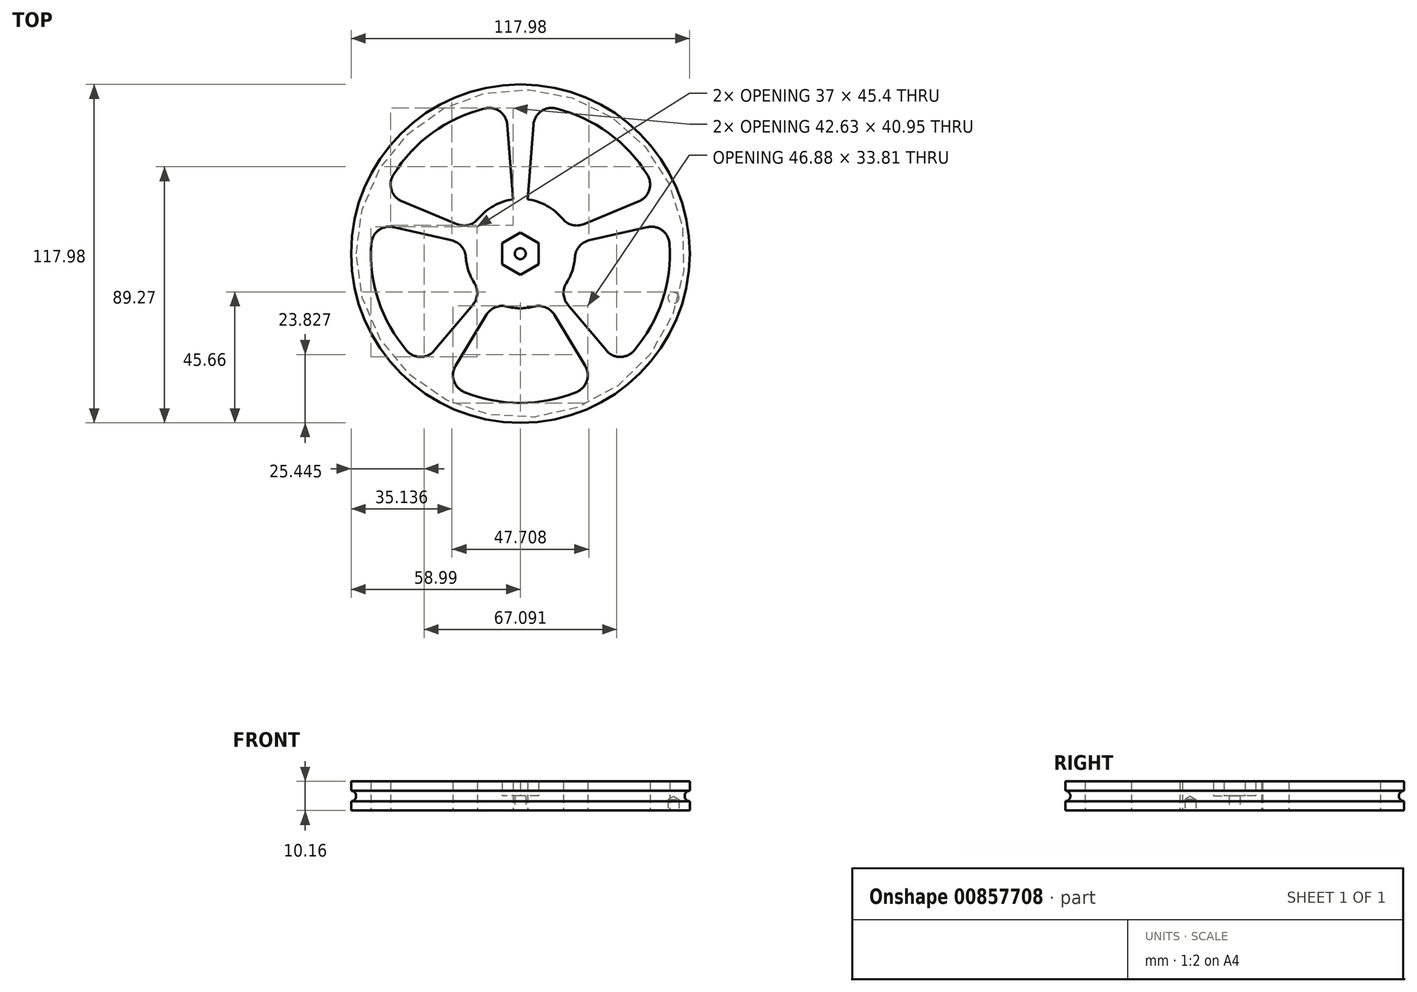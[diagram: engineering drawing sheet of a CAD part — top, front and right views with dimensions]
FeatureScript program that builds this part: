
annotation { "Feature Type Name" : "Feature", "Feature Type Description" : "" }
export const myFeature = defineFeature(function(context is Context, id is Id, definition is map)
    precondition{}
    {
        {
            var Q0;
            Q0=qCreatedBy(makeId("Top.planeOp"),FACE);
            var sketch = newSketch(context, id + "F0", { "sketchPlane" : qUnion([Q0])});
            skLineSegment(sketch, "E0.0", {"start": v(-0.03, -7.4) * mm, "end": v(-6.4, -3.71) * mm});
            skLineSegment(sketch, "E0.1", {"start": v(-6.4, -3.71) * mm, "end": v(-6.4, 3.65) * mm});
            skLineSegment(sketch, "E0.2", {"start": v(-6.4, 3.65) * mm, "end": v(-0.03, 7.34) * mm});
            skLineSegment(sketch, "E0.3", {"start": v(-0.03, 7.34) * mm, "end": v(6.35, 3.65) * mm});
            skLineSegment(sketch, "E0.4", {"start": v(6.35, 3.65) * mm, "end": v(6.35, -3.71) * mm});
            skLineSegment(sketch, "E0.5", {"start": v(6.35, -3.71) * mm, "end": v(-0.03, -7.4) * mm});
            skCircle(sketch, "E1", {"center": v(-0.03, -0.03) * mm, "radius": 1.9 * mm});
            skCircle(sketch, "E2", {"center": v(0, 0) * mm, "radius": 59 * mm});
            skArc(sketch, "E3", {"start": v(44.24, 27.46) * mm, "mid": v(30.58, 42.14) * mm, "end": v(12.39, 50.57) * mm});
            skArc(sketch, "E4", {"start": v(-4.77, -18.44) * mm, "mid": v(0, -19.05) * mm, "end": v(4.77, -18.44) * mm});
            skLineSegment(sketch, "E5", {"start": v(0, 0) * mm, "end": v(0, 52.07) * mm, "construction": true});
            skLineSegment(sketch, "E6", {"start": v(16.52, -17.8) * mm, "end": v(29.91, -33.76) * mm});
            skLineSegment(sketch, "E7", {"start": v(22.05, 10.27) * mm, "end": v(41.28, 18.24) * mm});
            skLineSegment(sketch, "E8.MirrorCS", {"start": v(11.79, -21.3) * mm, "end": v(22.56, -39.1) * mm});
            skLineSegment(sketch, "E9.MirrorCS", {"start": v(23.94, 4.6) * mm, "end": v(44.21, 9.2) * mm});
            skLineSegment(sketch, "E10", {"start": v(4.55, 44.9) * mm, "end": v(2.54, 18.88) * mm});
            skLineSegment(sketch, "E11.MirrorCS", {"start": v(-4.55, 44.9) * mm, "end": v(-2.54, 18.88) * mm});
            skLineSegment(sketch, "E12.MirrorCS", {"start": v(-22.05, 10.27) * mm, "end": v(-41.28, 18.24) * mm});
            skLineSegment(sketch, "E13.MirrorCS", {"start": v(-23.94, 4.6) * mm, "end": v(-44.21, 9.2) * mm});
            skLineSegment(sketch, "E14.MirrorCS", {"start": v(-16.52, -17.8) * mm, "end": v(-29.91, -33.76) * mm});
            skLineSegment(sketch, "E15.MirrorCS", {"start": v(-11.79, -21.3) * mm, "end": v(-22.56, -39.1) * mm});
            skArc(sketch, "E16.trimOffspring", {"start": v(39.6, -33.8) * mm, "mid": v(49.42, -16.39) * mm, "end": v(51.96, 3.44) * mm});
            skArc(sketch, "E17.trimOffspring", {"start": v(-19.5, -48.28) * mm, "mid": v(0, -52.07) * mm, "end": v(19.5, -48.28) * mm});
            skArc(sketch, "E18.trimOffspring", {"start": v(-51.96, 3.44) * mm, "mid": v(-49.42, -16.39) * mm, "end": v(-39.6, -33.8) * mm});
            skArc(sketch, "E19.trimOffspring", {"start": v(-12.39, 50.57) * mm, "mid": v(-30.58, 42.14) * mm, "end": v(-44.24, 27.46) * mm});
            skArc(sketch, "E20.trimOffspring", {"start": v(-19.01, -1.2) * mm, "mid": v(-18.1, -5.93) * mm, "end": v(-16.04, -10.28) * mm});
            skArc(sketch, "E21.trimOffspring", {"start": v(-2.54, 18.88) * mm, "mid": v(-9.27, 16.64) * mm, "end": v(-14.71, 12.1) * mm});
            skArc(sketch, "E22.trimOffspring", {"start": v(14.71, 12.1) * mm, "mid": v(9.27, 16.64) * mm, "end": v(2.54, 18.88) * mm});
            skPoint(sketch, "E23.visualSharp", {"position": v(-47.7, 20.9) * mm});
            skArc(sketch, "E23.filletArc", {"start": v(-44.24, 27.46) * mm, "mid": v(-44.9, 22.17) * mm, "end": v(-41.28, 18.24) * mm});
            skPoint(sketch, "E24.visualSharp", {"position": v(-50.95, 10.74) * mm});
            skArc(sketch, "E24.filletArc", {"start": v(-44.21, 9.2) * mm, "mid": v(-49.42, 8.1) * mm, "end": v(-51.96, 3.44) * mm});
            skPoint(sketch, "E25.visualSharp", {"position": v(-34.4, -39.1) * mm});
            skArc(sketch, "E25.filletArc", {"start": v(-39.6, -33.8) * mm, "mid": v(-34.75, -36.03) * mm, "end": v(-29.91, -33.76) * mm});
            skPoint(sketch, "E26.visualSharp", {"position": v(-26.15, -45.03) * mm});
            skArc(sketch, "E26.filletArc", {"start": v(-22.56, -39.1) * mm, "mid": v(-23.15, -44.4) * mm, "end": v(-19.5, -48.28) * mm});
            skPoint(sketch, "E27.visualSharp", {"position": v(26.15, -45.03) * mm});
            skArc(sketch, "E27.filletArc", {"start": v(19.5, -48.28) * mm, "mid": v(23.15, -44.4) * mm, "end": v(22.56, -39.1) * mm});
            skPoint(sketch, "E28.visualSharp", {"position": v(34.4, -39.1) * mm});
            skArc(sketch, "E28.filletArc", {"start": v(29.91, -33.76) * mm, "mid": v(34.75, -36.03) * mm, "end": v(39.6, -33.8) * mm});
            skPoint(sketch, "E29.visualSharp", {"position": v(50.95, 10.74) * mm});
            skArc(sketch, "E29.filletArc", {"start": v(51.96, 3.44) * mm, "mid": v(49.42, 8.1) * mm, "end": v(44.21, 9.2) * mm});
            skPoint(sketch, "E30.visualSharp", {"position": v(47.7, 20.9) * mm});
            skArc(sketch, "E30.filletArc", {"start": v(41.28, 18.24) * mm, "mid": v(44.9, 22.17) * mm, "end": v(44.24, 27.46) * mm});
            skPoint(sketch, "E31.visualSharp", {"position": v(5.08, 51.82) * mm});
            skArc(sketch, "E31.filletArc", {"start": v(12.39, 50.57) * mm, "mid": v(7.15, 49.55) * mm, "end": v(4.55, 44.9) * mm});
            skPoint(sketch, "E32.visualSharp", {"position": v(-5.08, 51.82) * mm});
            skArc(sketch, "E32.filletArc", {"start": v(-4.55, 44.9) * mm, "mid": v(-7.15, 49.55) * mm, "end": v(-12.39, 50.57) * mm});
            skPoint(sketch, "E33.visualSharp", {"position": v(-17.17, 8.25) * mm});
            skArc(sketch, "E33.filletArc", {"start": v(-22.05, 10.27) * mm, "mid": v(-18.08, 9.98) * mm, "end": v(-14.71, 12.1) * mm});
            skPoint(sketch, "E34.visualSharp", {"position": v(-18.74, 3.42) * mm});
            skArc(sketch, "E34.filletArc", {"start": v(-19.01, -1.2) * mm, "mid": v(-20.51, 2.52) * mm, "end": v(-23.94, 4.6) * mm});
            skPoint(sketch, "E35.visualSharp", {"position": v(-13.15, -13.78) * mm});
            skArc(sketch, "E35.filletArc", {"start": v(-16.52, -17.8) * mm, "mid": v(-15.04, -14.12) * mm, "end": v(-16.04, -10.28) * mm});
            skPoint(sketch, "E36.visualSharp", {"position": v(-9.04, -16.77) * mm});
            skArc(sketch, "E36.filletArc", {"start": v(-4.77, -18.44) * mm, "mid": v(-8.75, -18.71) * mm, "end": v(-11.79, -21.3) * mm});
            skPoint(sketch, "E37.visualSharp", {"position": v(18.74, 3.42) * mm});
            skArc(sketch, "E37.filletArc", {"start": v(23.94, 4.6) * mm, "mid": v(20.51, 2.52) * mm, "end": v(19.01, -1.2) * mm});
            skPoint(sketch, "E38.visualSharp", {"position": v(17.17, 8.25) * mm});
            skArc(sketch, "E38.filletArc", {"start": v(14.71, 12.1) * mm, "mid": v(18.08, 9.98) * mm, "end": v(22.05, 10.27) * mm});
            skArc(sketch, "E39.trimOffspring", {"start": v(16.04, -10.28) * mm, "mid": v(18.1, -5.93) * mm, "end": v(19.01, -1.2) * mm});
            skPoint(sketch, "E40.visualSharp", {"position": v(9.04, -16.77) * mm});
            skArc(sketch, "E40.filletArc", {"start": v(11.79, -21.3) * mm, "mid": v(8.75, -18.71) * mm, "end": v(4.77, -18.44) * mm});
            skPoint(sketch, "E41.visualSharp", {"position": v(13.15, -13.78) * mm});
            skArc(sketch, "E41.filletArc", {"start": v(16.04, -10.28) * mm, "mid": v(15.04, -14.12) * mm, "end": v(16.52, -17.8) * mm});
            skPoint(sketch, "E42.endSnap0", {"position": v(49.42, -16.39) * mm});
            skPoint(sketch, "E43", {"position": v(53.34, -15.43) * mm});
            skCircle(sketch, "E44", {"center": v(53.34, -15.43) * mm, "radius": 1.9 * mm});
            skSolve(sketch);
        }
        {
            var Q0;
            Q0=makeQuery(id+"F0.imprint","IMPRINT",FACE,{"disambiguationData":[TD([[makeQuery(id+"F0.imprint","IMPRINT",EDGE,{"derivedFrom":sQuery(id+"F0.wireOp",EDGE,"E0.0")}),-1.0]])]});
            extrude(context, id + "F1", {"entities" : qUnion([Q0]), "depth" : 5.08 * mm, "offsetDistance" : 25.4 * mm});
        }
        {
            var Q0;
            Q0=makeQuery(id+"F0.imprint","IMPRINT",FACE,{"disambiguationData":[TD([[makeQuery(id+"F0.imprint","IMPRINT",EDGE,{"derivedFrom":sQuery(id+"F0.wireOp",EDGE,"E0.0")}),1.0]])]});
            var Q1;
            Q1=makeQuery(id+"F0.imprint","IMPRINT",FACE,{"disambiguationData":[TD([[makeQuery(id+"F0.imprint","IMPRINT",EDGE,{"derivedFrom":sQuery(id+"F0.wireOp",EDGE,"E44")}),1.0]])]});
            extrude(context, id + "F2", {"entities" : qUnion([Q0, Q1]), "operationType" : NewBodyOperationType.ADD, "depth" : 10.16 * mm, "offsetDistance" : 25.4 * mm});
        }
        {
            var Q0;
            Q0=qCreatedBy(makeId("Front.planeOp"),FACE);
            var sketch = newSketch(context, id + "F3", { "sketchPlane" : qUnion([Q0])});
            skCircle(sketch, "E45", {"center": v(59.06, 5.08) * mm, "radius": 1.84 * mm});
            skSolve(sketch);
        }
        {
            var Q0;
            Q0=qCreatedBy(makeId("Front.planeOp"),FACE);
            var sketch = newSketch(context, id + "F4", { "sketchPlane" : qUnion([Q0])});
            skLineSegment(sketch, "E46", {"start": v(0, -19.08) * mm, "end": v(0, 27.89) * mm});
            skSolve(sketch);
        }
        {
            var Q0;
            Q0 = qSketchRegion(id + "F3", true);
            var Q1;
            Q1=sQuery(id+"F4.wireOp",EDGE,"E46");
            revolve(context, id + "F5", {"surfaceOperationType" : NewSurfaceOperationType.NEW, "entities" : qUnion([Q0]), "axis" : qUnion([Q1]), "revolveType" : RevolveType.FULL});
        }
        {
            var Q0;
            Q0=makeQuery(id+"F5.opRevolve","SWEPT_BODY",BODY,{"disambiguationData":[OSD([sQuery(id+"F3.wireOp",EDGE,"E45")])]});
            var Q1;
            Q1=makeQuery(id+"F1.opExtrude","SWEPT_BODY",BODY,{"disambiguationData":[OSD([sQuery(id+"F0.wireOp",EDGE,"E0.0"),sQuery(id+"F0.wireOp",EDGE,"E0.1"),sQuery(id+"F0.wireOp",EDGE,"E0.2"),sQuery(id+"F0.wireOp",EDGE,"E0.3"),sQuery(id+"F0.wireOp",EDGE,"E0.4"),sQuery(id+"F0.wireOp",EDGE,"E0.5"),sQuery(id+"F0.wireOp",EDGE,"E1")])]});
            booleanBodies(context, id + "F6", {"operationType" : BooleanOperationType.SUBTRACTION, "tools" : qUnion([Q0]), "targets" : qUnion([Q1])});
        }
        {
            var Q0;
            Q0=sQuery(id+"F0.wireOp",VERTEX,"E43");
            var Q1;
            Q1=makeQuery(id+"F1.opExtrude","SWEPT_BODY",BODY,{"disambiguationData":[OSD([sQuery(id+"F0.wireOp",EDGE,"E0.0"),sQuery(id+"F0.wireOp",EDGE,"E0.1"),sQuery(id+"F0.wireOp",EDGE,"E0.2"),sQuery(id+"F0.wireOp",EDGE,"E0.3"),sQuery(id+"F0.wireOp",EDGE,"E0.4"),sQuery(id+"F0.wireOp",EDGE,"E0.5"),sQuery(id+"F0.wireOp",EDGE,"E1")])]});
            hole(context, id + "F7", {"style" : HoleStyle.SIMPLE, "endStyle" : HoleEndStyle.BLIND, "oppositeDirection" : true, "holeDiameter" : 3.8 * mm, "majorDiameter" : 6.35 * mm, "holeDepth" : 3.8 * mm, "isTappedThrough" : true, "tappedDepth" : 12.7 * mm, "tapClearance" : 3, "locations" : qUnion([Q0]), "scope" : qUnion([Q1])});
        }
    });
